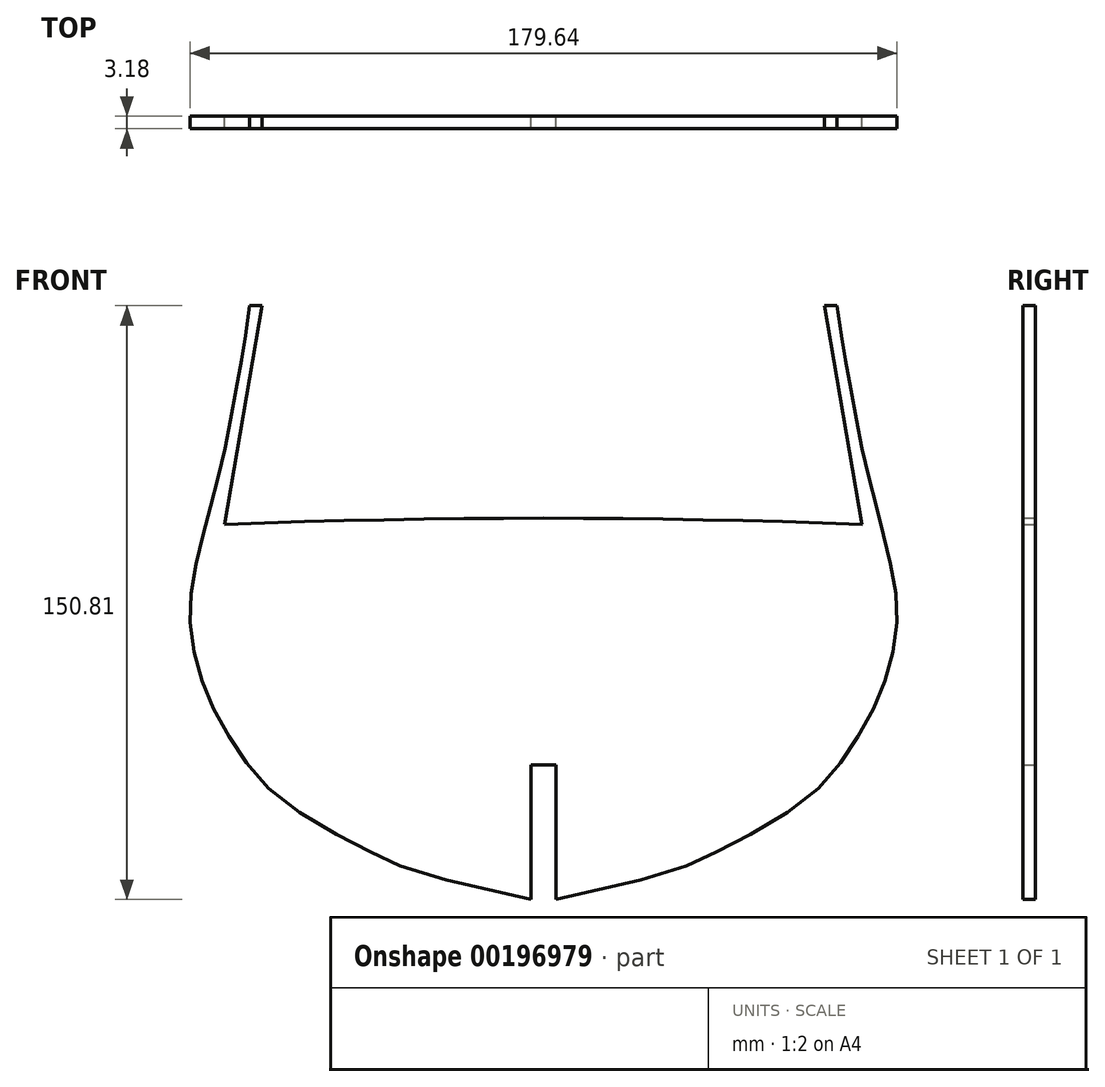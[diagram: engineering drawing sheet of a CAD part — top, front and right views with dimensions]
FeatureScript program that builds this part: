
annotation { "Feature Type Name" : "Feature", "Feature Type Description" : "" }
export const myFeature = defineFeature(function(context is Context, id is Id, definition is map)
    precondition{}
    {
        {
            var Q0;
            Q0=qCreatedBy(makeId("Front.planeOp"),FACE);
            var sketch = newSketch(context, id + "F0", { "sketchPlane" : qUnion([Q0])});
            skLineSegment(sketch, "E0", {"start": v(0, 0) * mm, "end": v(0, -61.12) * mm, "construction": true});
            skLineSegment(sketch, "E1", {"start": v(0, -61.12) * mm, "end": v(3.18, -61.12) * mm});
            skLineSegment(sketch, "E2", {"start": v(3.18, -61.12) * mm, "end": v(3.18, -95.25) * mm});
            skLineSegment(sketch, "E3", {"start": v(3.18, -95.25) * mm, "end": v(-3.17, -95.25) * mm, "construction": true});
            skLineSegment(sketch, "E4", {"start": v(-3.17, -95.25) * mm, "end": v(-3.17, -61.12) * mm});
            skLineSegment(sketch, "E5", {"start": v(-3.17, -61.12) * mm, "end": v(0, -61.12) * mm});
            skFitSpline(sketch, "E6", {"points": [v(3.18, -95.25) * mm, v(45.24, -82.55) * mm, v(66.68, -69.85) * mm, v(77.79, -57.15) * mm, v(84.93, -44.45) * mm, v(88.9, -31.75) * mm, v(89.7, -19.05) * mm, v(87.31, -6.35) * mm, v(84.14, 6.35) * mm, v(80.96, 19.05) * mm, v(78.58, 31.75) * mm, v(76.2, 44.45) * mm, v(74.61, 55.56) * mm], "startDerivative": vector(657, 138.31) * mm, "endDerivative": vector(-34.22, 239.53) * mm});
            skLineSegment(sketch, "E7", {"start": v(0, 0) * mm, "end": v(0, 1.59) * mm, "construction": true});
            skLineSegment(sketch, "E8", {"start": v(80.96, 0) * mm, "end": v(0, 0) * mm, "construction": true});
            skLineSegment(sketch, "E9", {"start": v(0, 0) * mm, "end": v(-80.96, 0) * mm, "construction": true});
            skArc(sketch, "E10", {"start": v(80.96, 0) * mm, "mid": v(0, 1.59) * mm, "end": v(-80.96, 0) * mm});
            skLineSegment(sketch, "E11", {"start": v(74.61, 55.56) * mm, "end": v(71.44, 55.56) * mm});
            skLineSegment(sketch, "E12", {"start": v(71.44, 55.56) * mm, "end": v(80.96, 0) * mm});
            skLineSegment(sketch, "E13.MirrorCS", {"start": v(-71.44, 55.56) * mm, "end": v(-80.96, 0) * mm});
            skLineSegment(sketch, "E14.MirrorCS", {"start": v(-74.61, 55.56) * mm, "end": v(-71.44, 55.56) * mm});
            skFitSpline(sketch, "E15.MirrorCS", {"points": [v(-3.18, -95.25) * mm, v(-45.24, -82.55) * mm, v(-66.68, -69.85) * mm, v(-77.79, -57.15) * mm, v(-84.93, -44.45) * mm, v(-88.9, -31.75) * mm, v(-89.7, -19.05) * mm, v(-87.31, -6.35) * mm, v(-84.14, 6.35) * mm, v(-80.96, 19.05) * mm, v(-78.58, 31.75) * mm, v(-76.2, 44.45) * mm, v(-74.61, 55.56) * mm], "startDerivative": vector(-657, 138.31) * mm, "endDerivative": vector(34.22, 239.53) * mm});
            skSolve(sketch);
        }
        {
            var Q0;
            Q0=makeQuery(id+"F0.imprint","IMPRINT",FACE,{"disambiguationData":[TD([[makeQuery(id+"F0.imprint","IMPRINT",EDGE,{"derivedFrom":sQuery(id+"F0.wireOp",EDGE,"E1")}),1.0]])]});
            extrude(context, id + "F1", {"entities" : qUnion([Q0]), "endBound" : BoundingType.SYMMETRIC, "depth" : 3.17 * mm});
        }
    });
